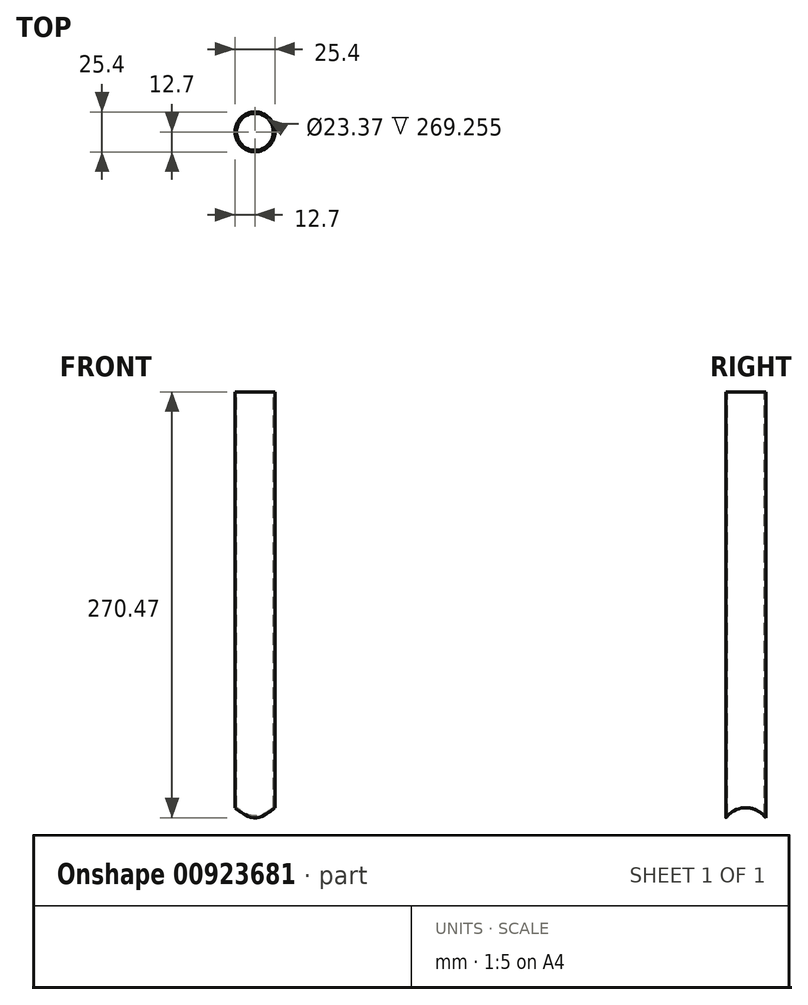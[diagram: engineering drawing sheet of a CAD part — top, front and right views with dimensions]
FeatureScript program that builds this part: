
annotation { "Feature Type Name" : "Feature", "Feature Type Description" : "" }
export const myFeature = defineFeature(function(context is Context, id is Id, definition is map)
    precondition{}
    {
        {
            var Q0;
            Q0=qCreatedBy(makeId("Top.planeOp"),FACE);
            var sketch = newSketch(context, id + "F0", { "sketchPlane" : qUnion([Q0])});
            skCircle(sketch, "E0", {"center": v(0, 0) * mm, "radius": 12.7 * mm});
            skSolve(sketch);
        }
        {
            var Q0;
            Q0=makeQuery(id+"F0.imprint","IMPRINT",FACE,{"disambiguationData":[TD([[makeQuery(id+"F0.imprint","IMPRINT",EDGE,{"derivedFrom":sQuery(id+"F0.wireOp",EDGE,"E0")}),1.0]])]});
            extrude(context, id + "F1", {"entities" : qUnion([Q0]), "depth" : 280 * mm, "offsetDistance" : 25 * mm});
        }
        {
            var Q0;
            Q0=qCreatedBy(makeId("Right.planeOp"),FACE);
            var sketch = newSketch(context, id + "F2", { "sketchPlane" : qUnion([Q0])});
            skCircle(sketch, "E1", {"center": v(0, 0) * mm, "radius": 15.88 * mm});
            skSolve(sketch);
        }
        {
            var Q0;
            Q0=qSketchRegion(id+"F2",true);
            extrude(context, id + "F3", {"entities" : qUnion([Q0]), "operationType" : NewBodyOperationType.REMOVE, "endBound" : BoundingType.SYMMETRIC, "oppositeDirection" : true, "depth" : 100 * mm, "offsetDistance" : 25 * mm});
        }
        {
            var Q0;
            Q0=makeQuery(id+"F1.opExtrude","CAP_FACE",FACE,{"disambiguationData":[OSD([sQuery(id+"F0.wireOp",EDGE,"E0")])],"isStart":false});
            var sketch = newSketch(context, id + "F4", { "sketchPlane" : qUnion([Q0])});
            skCircle(sketch, "E2", {"center": v(0, 0) * mm, "radius": 11.68 * mm});
            skLineSegment(sketch, "E3", {"start": v(11.68, 0) * mm, "end": v(12.7, 0) * mm, "construction": true});
            skSolve(sketch);
        }
        {
            var Q0;
            Q0=qSketchRegion(id+"F4",true);
            extrude(context, id + "F5", {"entities" : qUnion([Q0]), "operationType" : NewBodyOperationType.REMOVE, "endBound" : BoundingType.THROUGH_ALL, "oppositeDirection" : true, "depth" : 25 * mm, "offsetDistance" : 25 * mm});
        }
    });
